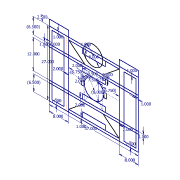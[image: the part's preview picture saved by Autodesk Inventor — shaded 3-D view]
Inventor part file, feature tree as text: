
AUTODESK INVENTOR PART (.ipt)
format: ipt  version: 2012 (Build 160160000, 160)  size: 109,568 bytes
history: native  units: in
note: dims shown in document units (in); Inventor stores cm internally (conversion verified against a paired STEP export)
features: sketch x1
ambient origin geometry x8: Origin, YZ Plane, XZ Plane, XY Plane, X Axis, Y Axis, Z Axis, Center Point
feature tree (1):
  sketch  "Sketch1"  dims[d0=37.0in d1=27.0in d2=8.0in d3=8.0in d4=1.0in d5=1.0in d6=1.0in d7=2.0in d9=1.0in d11=1.0in d12=1.0in d13=2.0in d14=1.0in d15=1.0in d16=1.0in d17=1.0in d18=12.0in d28=7.5in d29=2.0in d30=9.5in d31=2.0in d32=1.0in d33=6.5in d34=6.5in d35=2.0in d36=2.0in d37=1.0in d40=6.75in d41=6.75in d42=8.0in d43=2.5in d44=8.0in]
